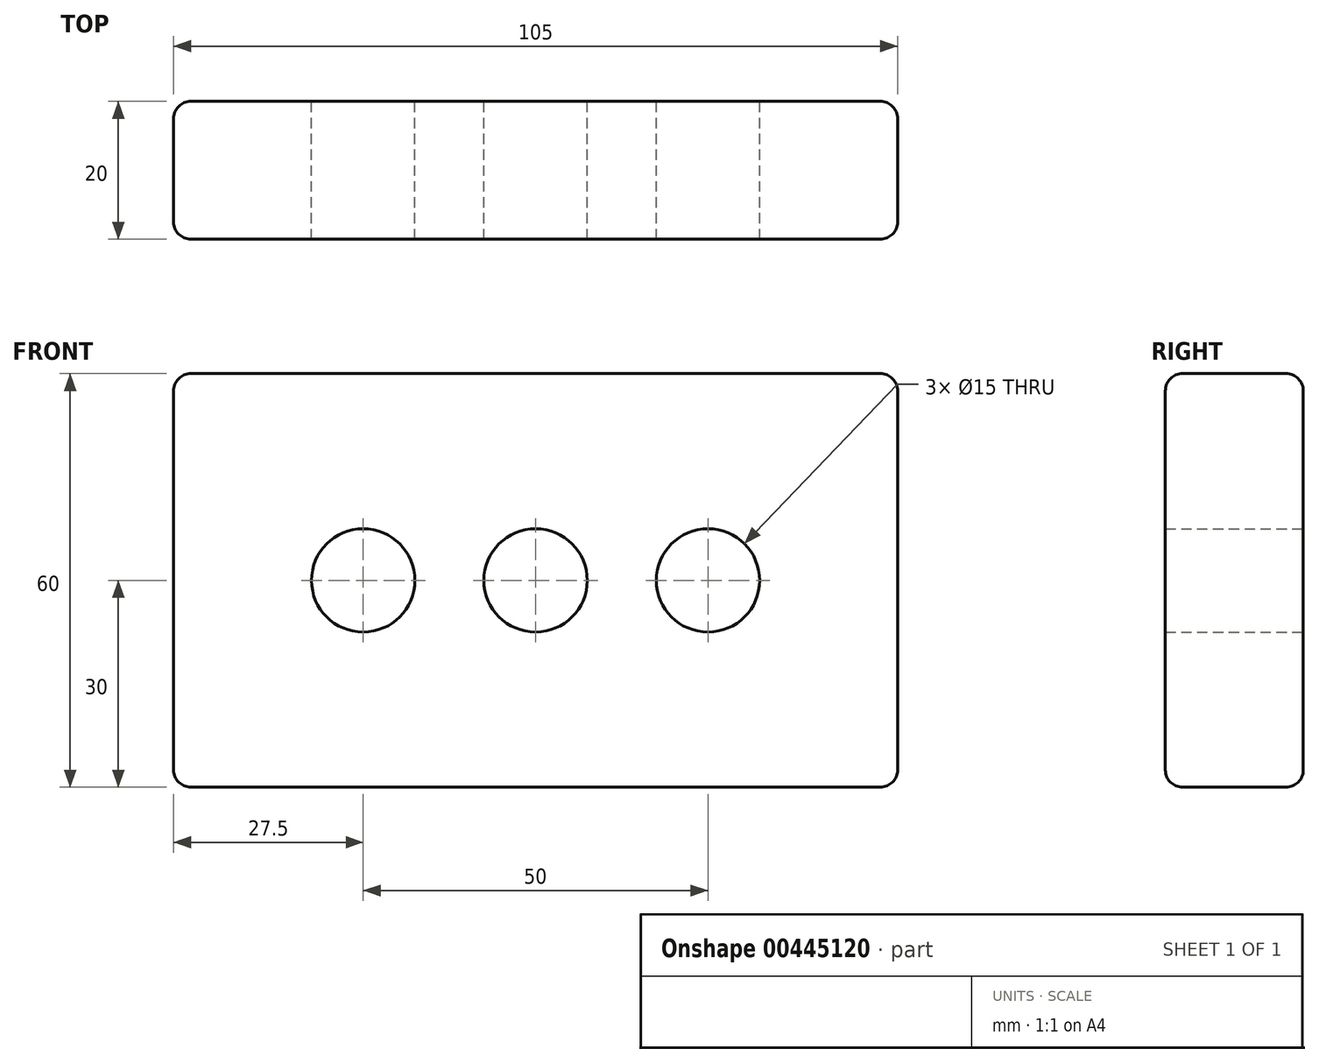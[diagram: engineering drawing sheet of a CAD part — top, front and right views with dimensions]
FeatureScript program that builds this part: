
annotation { "Feature Type Name" : "Feature", "Feature Type Description" : "" }
export const myFeature = defineFeature(function(context is Context, id is Id, definition is map)
    precondition{}
    {
        {
            var Q0;
            Q0=qCreatedBy(makeId("Front.planeOp"),FACE);
            var sketch = newSketch(context, id + "F0", { "sketchPlane" : qUnion([Q0])});
            skLineSegment(sketch, "E0.bottom", {"start": v(52.5, -30) * mm, "end": v(-52.5, -30) * mm});
            skLineSegment(sketch, "E0.top", {"start": v(52.5, 30) * mm, "end": v(-52.5, 30) * mm});
            skLineSegment(sketch, "E0.left", {"start": v(52.5, -30) * mm, "end": v(52.5, 30) * mm});
            skLineSegment(sketch, "E0.right", {"start": v(-52.5, -30) * mm, "end": v(-52.5, 30) * mm});
            skPoint(sketch, "E0.middle", {"position": v(0, 0) * mm});
            skCircle(sketch, "E1", {"center": v(0, 0) * mm, "radius": 7.5 * mm});
            skLineSegment(sketch, "E2", {"start": v(-25, 0) * mm, "end": v(0, 0) * mm});
            skLineSegment(sketch, "E3", {"start": v(0, 0) * mm, "end": v(25, 0) * mm});
            skCircle(sketch, "E4", {"center": v(-25, 0) * mm, "radius": 7.5 * mm});
            skCircle(sketch, "E5", {"center": v(25, 0) * mm, "radius": 7.5 * mm});
            skSolve(sketch);
        }
        {
            var Q0;
            Q0=makeQuery(id+"F0.imprint","IMPRINT",FACE,{"disambiguationData":[TD([[makeQuery(id+"F0.imprint","IMPRINT",EDGE,{"derivedFrom":sQuery(id+"F0.wireOp",EDGE,"E0.bottom")}),-1.0]])]});
            extrude(context, id + "F1", {"entities" : qUnion([Q0]), "depth" : 20 * mm});
        }
        {
            var Q0;
            Q0=makeQuery(id+"F1.opExtrude","CAP_EDGE",EDGE,{"disambiguationData":[OSD([sQuery(id+"F0.wireOp",EDGE,"E0.bottom")])],"isStart":false});
            var Q1;
            Q1=makeQuery(id+"F1.opExtrude","CAP_EDGE",EDGE,{"disambiguationData":[OSD([sQuery(id+"F0.wireOp",EDGE,"E0.left")])],"isStart":false});
            var Q2;
            Q2=makeQuery(id+"F1.opExtrude","CAP_EDGE",EDGE,{"disambiguationData":[OSD([sQuery(id+"F0.wireOp",EDGE,"E0.top")])],"isStart":false});
            var Q3;
            Q3=makeQuery(id+"F1.opExtrude","CAP_EDGE",EDGE,{"disambiguationData":[OSD([sQuery(id+"F0.wireOp",EDGE,"E0.right")])],"isStart":false});
            var Q4;
            Q4=makeQuery(id+"F1.opExtrude","SWEPT_EDGE",EDGE,{"disambiguationData":[OSD([sQuery(id+"F0.wireOp",EDGE,"E0.top"),sQuery(id+"F0.wireOp",EDGE,"E0.right")])]});
            var Q5;
            Q5=makeQuery(id+"F1.opExtrude","SWEPT_FACE",FACE,{"disambiguationData":[OSD([sQuery(id+"F0.wireOp",EDGE,"E0.right")])]});
            var Q6;
            Q6=makeQuery(id+"F1.opExtrude","CAP_EDGE",EDGE,{"disambiguationData":[OSD([sQuery(id+"F0.wireOp",EDGE,"E0.bottom")])],"isStart":true});
            var Q7;
            Q7=makeQuery(id+"F1.opExtrude","SWEPT_EDGE",EDGE,{"disambiguationData":[OSD([sQuery(id+"F0.wireOp",EDGE,"E0.bottom"),sQuery(id+"F0.wireOp",EDGE,"E0.left")])]});
            var Q8;
            Q8=makeQuery(id+"F1.opExtrude","SWEPT_EDGE",EDGE,{"disambiguationData":[OSD([sQuery(id+"F0.wireOp",EDGE,"E0.top"),sQuery(id+"F0.wireOp",EDGE,"E0.left")])]});
            var Q9;
            Q9=makeQuery(id+"F1.opExtrude","CAP_EDGE",EDGE,{"disambiguationData":[OSD([sQuery(id+"F0.wireOp",EDGE,"E0.left")])],"isStart":true});
            var Q10;
            Q10=makeQuery(id+"F1.opExtrude","CAP_EDGE",EDGE,{"disambiguationData":[OSD([sQuery(id+"F0.wireOp",EDGE,"E0.top")])],"isStart":true});
            fillet(context, id + "F2", {"entities" : qUnion([Q0, Q1, Q2, Q3, Q4, Q5, Q6, Q7, Q8, Q9, Q10]), "radius" : 2.5 * mm, "tangentPropagation" : true, "allowEdgeOverflow" : false});
        }
    });
